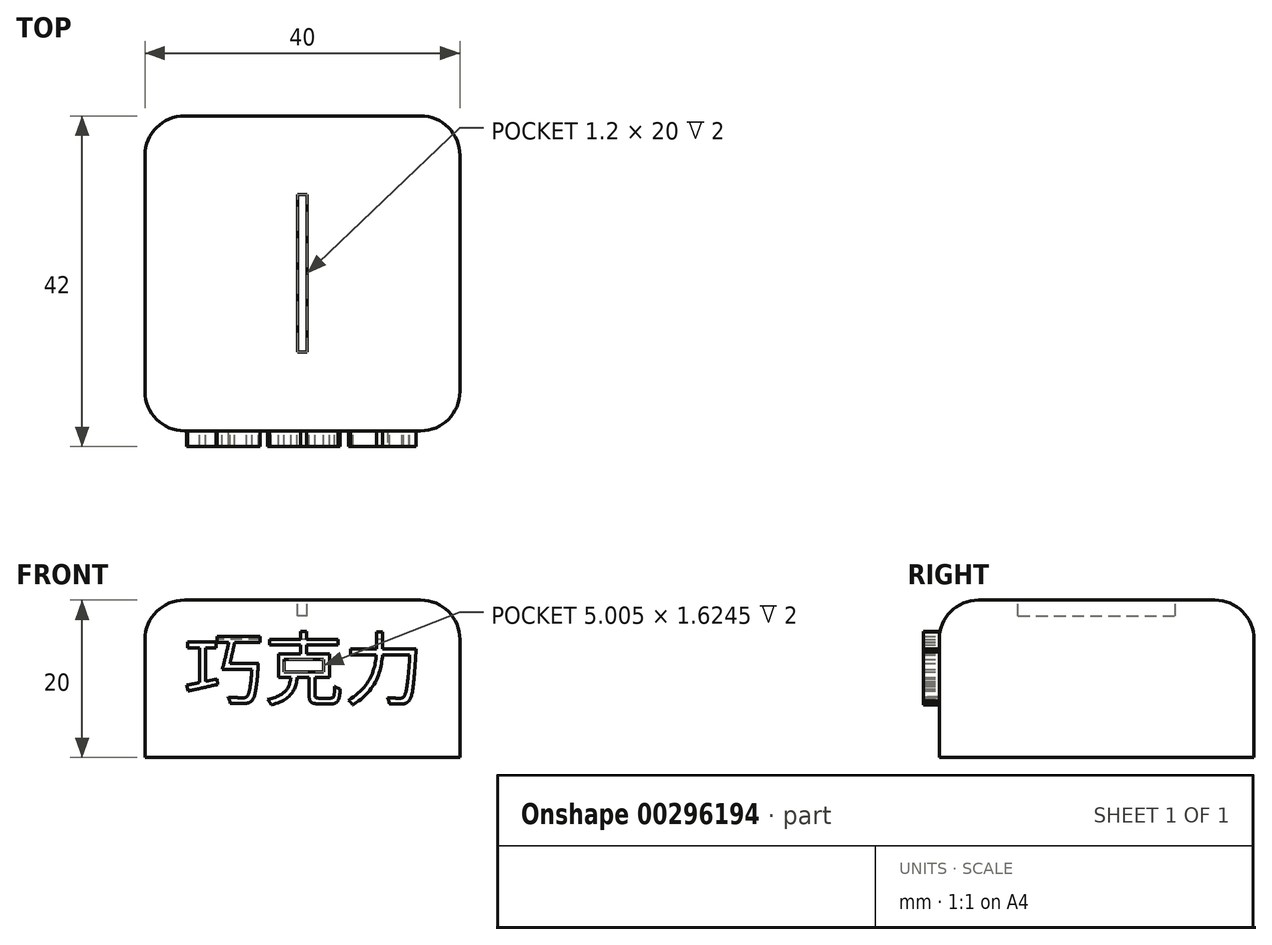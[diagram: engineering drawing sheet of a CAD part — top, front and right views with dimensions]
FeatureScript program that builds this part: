
annotation { "Feature Type Name" : "Feature", "Feature Type Description" : "" }
export const myFeature = defineFeature(function(context is Context, id is Id, definition is map)
    precondition{}
    {
        {
            var Q0;
            Q0=qCreatedBy(makeId("Top.planeOp"),FACE);
            var sketch = newSketch(context, id + "F0", { "sketchPlane" : qUnion([Q0])});
            skLineSegment(sketch, "E0.bottom", {"start": v(20, -20) * mm, "end": v(-20, -20) * mm});
            skLineSegment(sketch, "E0.top", {"start": v(20, 20) * mm, "end": v(-20, 20) * mm});
            skLineSegment(sketch, "E0.left", {"start": v(20, -20) * mm, "end": v(20, 20) * mm});
            skLineSegment(sketch, "E0.right", {"start": v(-20, -20) * mm, "end": v(-20, 20) * mm});
            skPoint(sketch, "E0.middle", {"position": v(0, 0) * mm});
            skLineSegment(sketch, "E1.bottom", {"start": v(0.6, -10) * mm, "end": v(-0.6, -10) * mm});
            skLineSegment(sketch, "E1.top", {"start": v(0.6, 10) * mm, "end": v(-0.6, 10) * mm});
            skLineSegment(sketch, "E1.left", {"start": v(0.6, -10) * mm, "end": v(0.6, 10) * mm});
            skLineSegment(sketch, "E1.right", {"start": v(-0.6, -10) * mm, "end": v(-0.6, 10) * mm});
            skSolve(sketch);
        }
        {
            var Q0;
            Q0=makeQuery(id+"F0.imprint","IMPRINT",FACE,{"disambiguationData":[TD([[makeQuery(id+"F0.imprint","IMPRINT",EDGE,{"derivedFrom":sQuery(id+"F0.wireOp",EDGE,"E0.bottom")}),-1.0]])]});
            var Q1;
            Q1=makeQuery(id+"F0.imprint","IMPRINT",FACE,{"disambiguationData":[TD([[makeQuery(id+"F0.imprint","IMPRINT",EDGE,{"derivedFrom":sQuery(id+"F0.wireOp",EDGE,"E1.bottom")}),-1.0]])]});
            extrude(context, id + "F1", {"entities" : qUnion([Q0, Q1]), "oppositeDirection" : true, "depth" : 20 * mm});
        }
        {
            var Q0;
            Q0=makeQuery(id+"F0.imprint","IMPRINT",FACE,{"disambiguationData":[TD([[makeQuery(id+"F0.imprint","IMPRINT",EDGE,{"derivedFrom":sQuery(id+"F0.wireOp",EDGE,"E1.bottom")}),-1.0]])]});
            extrude(context, id + "F2", {"entities" : qUnion([Q0]), "operationType" : NewBodyOperationType.REMOVE, "oppositeDirection" : true, "depth" : 2 * mm});
        }
        {
            var Q0;
            Q0=makeQuery(id+"F2.boolean.opBoolean","COPY",EDGE,{"derivedFrom":makeQuery(id+"F2.opExtrude","CAP_EDGE",EDGE,{"disambiguationData":[OSD([sQuery(id+"F0.wireOp",EDGE,"E1.left")])],"isStart":true})});
            var Q1;
            Q1=makeQuery(id+"F2.boolean.opBoolean","COPY",EDGE,{"derivedFrom":makeQuery(id+"F2.opExtrude","CAP_EDGE",EDGE,{"disambiguationData":[OSD([sQuery(id+"F0.wireOp",EDGE,"E1.right")])],"isStart":true})});
            var Q2;
            Q2=makeQuery(id+"F1.opExtrude","SWEPT_EDGE",EDGE,{"disambiguationData":[OSD([sQuery(id+"F0.wireOp",EDGE,"E0.bottom"),sQuery(id+"F0.wireOp",EDGE,"E0.left")])]});
            var Q3;
            Q3=makeQuery(id+"F1.opExtrude","SWEPT_EDGE",EDGE,{"disambiguationData":[OSD([sQuery(id+"F0.wireOp",EDGE,"E0.top"),sQuery(id+"F0.wireOp",EDGE,"E0.left")])]});
            var Q4;
            Q4=makeQuery(id+"F1.opExtrude","CAP_EDGE",EDGE,{"disambiguationData":[OSD([sQuery(id+"F0.wireOp",EDGE,"E0.left")])],"isStart":true});
            var Q5;
            Q5=makeQuery(id+"F1.opExtrude","SWEPT_EDGE",EDGE,{"disambiguationData":[OSD([sQuery(id+"F0.wireOp",EDGE,"E0.bottom"),sQuery(id+"F0.wireOp",EDGE,"E0.right")])]});
            var Q6;
            Q6=makeQuery(id+"F1.opExtrude","SWEPT_EDGE",EDGE,{"disambiguationData":[OSD([sQuery(id+"F0.wireOp",EDGE,"E0.top"),sQuery(id+"F0.wireOp",EDGE,"E0.right")])]});
            var Q7;
            Q7=makeQuery(id+"F1.opExtrude","CAP_EDGE",EDGE,{"disambiguationData":[OSD([sQuery(id+"F0.wireOp",EDGE,"E0.top")])],"isStart":true});
            var Q8;
            Q8=makeQuery(id+"F1.opExtrude","CAP_EDGE",EDGE,{"disambiguationData":[OSD([sQuery(id+"F0.wireOp",EDGE,"E0.right")])],"isStart":true});
            var Q9;
            Q9=makeQuery(id+"F1.opExtrude","CAP_EDGE",EDGE,{"disambiguationData":[OSD([sQuery(id+"F0.wireOp",EDGE,"E0.bottom")])],"isStart":true});
            fillet(context, id + "F3", {"entities" : qUnion([Q0, Q1, Q2, Q3, Q4, Q5, Q6, Q7, Q8, Q9]), "radius" : 5 * mm, "tangentPropagation" : true, "allowEdgeOverflow" : false});
        }
        {
            var Q0;
            Q0=makeQuery(id+"F1.opExtrude","SWEPT_FACE",FACE,{"disambiguationData":[OSD([sQuery(id+"F0.wireOp",EDGE,"E0.bottom")])]});
            var sketch = newSketch(context, id + "F4", { "sketchPlane" : qUnion([Q0])});
            skText(sketch, "E2", { "text": "巧克力", "fontName": "NotoSansCJKtc-Regular.otf"});
            const initialGuessF4  = {"E2": [-0.01506, -0.0125, 1, 0, 0.00731]};
            skSetInitialGuess(sketch, initialGuessF4);
            skSolve(sketch);
        }
        {
            var Q0;
            Q0=qSketchRegion(id+"F4",true);
            extrude(context, id + "F5", {"entities" : qUnion([Q0]), "operationType" : NewBodyOperationType.ADD, "depth" : 2 * mm});
        }
    });
